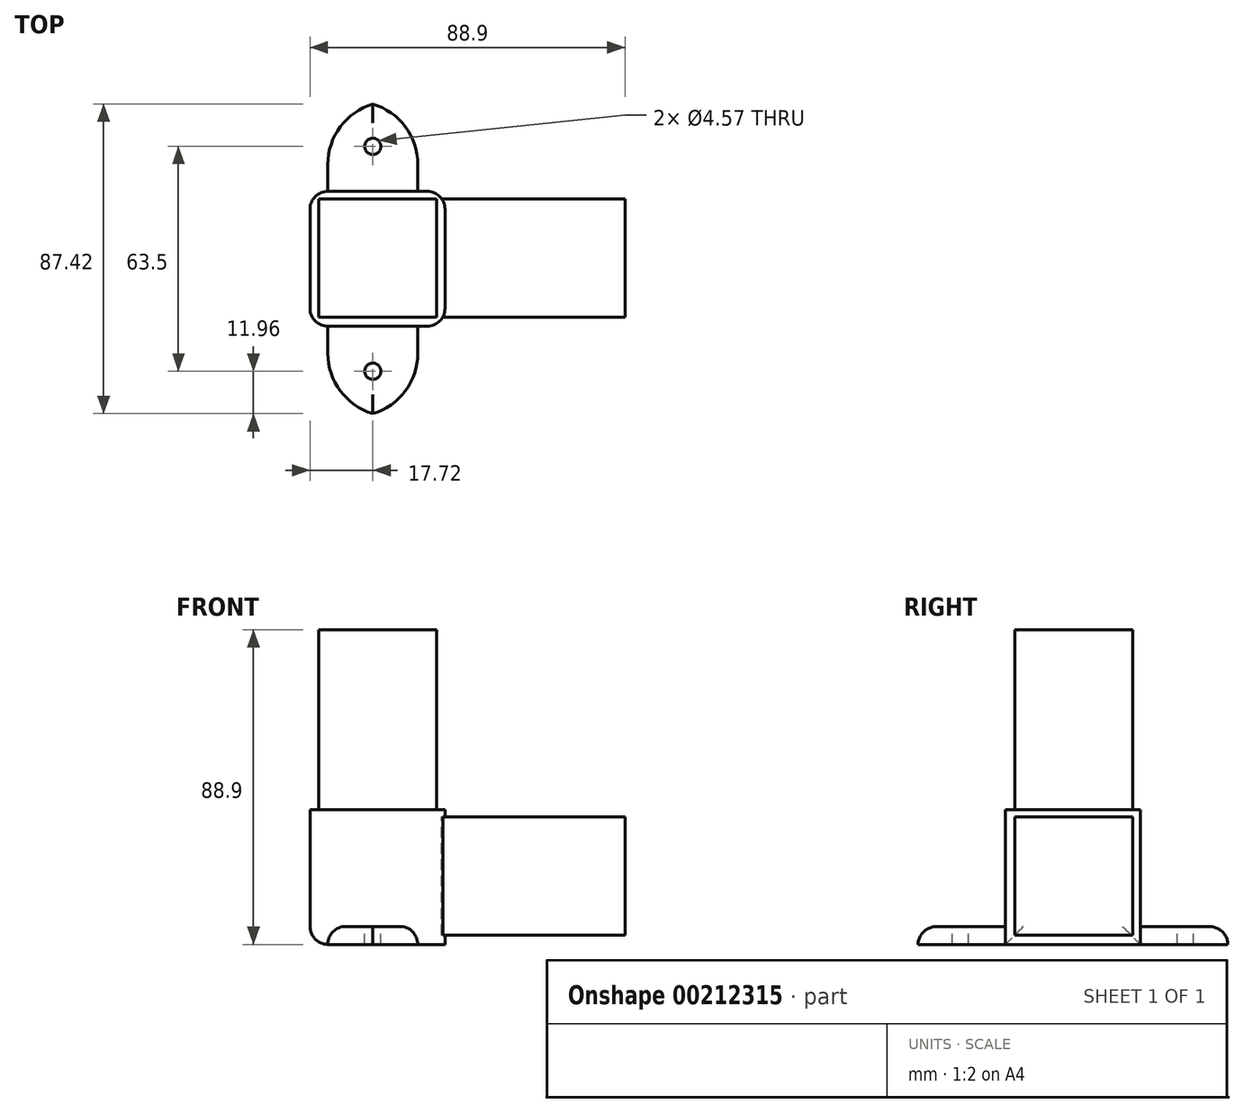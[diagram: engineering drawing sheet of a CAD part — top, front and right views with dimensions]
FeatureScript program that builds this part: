
annotation { "Feature Type Name" : "Feature", "Feature Type Description" : "" }
export const myFeature = defineFeature(function(context is Context, id is Id, definition is map)
    precondition{}
    {
        {
            var Q0;
            Q0=qCreatedBy(makeId("Front.planeOp"),FACE);
            var sketch = newSketch(context, id + "F0", { "sketchPlane" : qUnion([Q0])});
            skLineSegment(sketch, "E0.bottom", {"start": v(0.35, 8.9) * mm, "end": v(38.45, 8.9) * mm});
            skLineSegment(sketch, "E0.top", {"start": v(0.35, -29.2) * mm, "end": v(38.45, -29.2) * mm});
            skLineSegment(sketch, "E0.left", {"start": v(0.35, 8.9) * mm, "end": v(0.35, -29.2) * mm});
            skLineSegment(sketch, "E0.right", {"start": v(38.45, 8.9) * mm, "end": v(38.45, -29.2) * mm});
            skSolve(sketch);
        }
        {
            var Q0;
            Q0=makeQuery(id+"F0.imprint","IMPRINT",FACE,{"disambiguationData":[TD([[makeQuery(id+"F0.imprint","IMPRINT",EDGE,{"derivedFrom":sQuery(id+"F0.wireOp",EDGE,"E0.bottom")}),-1.0]])]});
            extrude(context, id + "F1", {"entities" : qUnion([Q0]), "depth" : 38.1 * mm});
        }
        {
            var Q0;
            Q0=makeQuery(id+"F1.opExtrude","SWEPT_FACE",FACE,{"disambiguationData":[OSD([sQuery(id+"F0.wireOp",EDGE,"E0.right")])]});
            var sketch = newSketch(context, id + "F2", { "sketchPlane" : qUnion([Q0])});
            skLineSegment(sketch, "E1.bottom", {"start": v(-35.49, 6.76) * mm, "end": v(-2.15, 6.76) * mm});
            skLineSegment(sketch, "E1.top", {"start": v(-35.49, -26.58) * mm, "end": v(-2.15, -26.58) * mm});
            skLineSegment(sketch, "E1.left", {"start": v(-35.49, 6.76) * mm, "end": v(-35.49, -26.58) * mm});
            skLineSegment(sketch, "E1.right", {"start": v(-2.15, 6.76) * mm, "end": v(-2.15, -26.58) * mm});
            skSolve(sketch);
        }
        {
            var Q0;
            Q0 = qSketchRegion(id + "F2", true);
            extrude(context, id + "F3", {"entities" : qUnion([Q0]), "operationType" : NewBodyOperationType.ADD, "depth" : 50.8 * mm});
        }
        {
            var Q0;
            Q0=makeQuery(id+"F1.opExtrude","SWEPT_FACE",FACE,{"disambiguationData":[OSD([sQuery(id+"F0.wireOp",EDGE,"E0.bottom")])]});
            var sketch = newSketch(context, id + "F4", { "sketchPlane" : qUnion([Q0])});
            skLineSegment(sketch, "E2.bottom", {"start": v(2.78, -35.49) * mm, "end": v(36.12, -35.49) * mm});
            skLineSegment(sketch, "E2.top", {"start": v(2.78, -2.15) * mm, "end": v(36.12, -2.15) * mm});
            skLineSegment(sketch, "E2.left", {"start": v(2.78, -35.49) * mm, "end": v(2.78, -2.15) * mm});
            skLineSegment(sketch, "E2.right", {"start": v(36.12, -35.49) * mm, "end": v(36.12, -2.15) * mm});
            skSolve(sketch);
        }
        {
            var Q0;
            Q0=makeQuery(id+"F4.imprint","IMPRINT",FACE,{"disambiguationData":[TD([[makeQuery(id+"F4.imprint","IMPRINT",EDGE,{"derivedFrom":sQuery(id+"F4.wireOp",EDGE,"E2.bottom")}),1.0]])]});
            var Q1;
            Q1=sQuery(id+"F4.wireOp",EDGE,"E2.top");
            var Q2;
            Q2=sQuery(id+"F4.wireOp",EDGE,"E2.left");
            var Q3;
            Q3=sQuery(id+"F4.wireOp",EDGE,"E2.right");
            extrude(context, id + "F5", {"entities" : qUnion([Q0]), "surfaceEntities" : qUnion([Q1, Q2, Q3]), "depth" : 50.8 * mm});
        }
        {
            var Q0;
            Q0=makeQuery(id+"F1.opExtrude","SWEPT_FACE",FACE,{"disambiguationData":[OSD([sQuery(id+"F0.wireOp",EDGE,"E0.top")])]});
            var sketch = newSketch(context, id + "F6", { "sketchPlane" : qUnion([Q0])});
            skLineSegment(sketch, "E3.bottom", {"start": v(5.37, 38.1) * mm, "end": v(30.77, 38.1) * mm});
            skLineSegment(sketch, "E3.top", {"start": v(5.37, 63.5) * mm, "end": v(30.77, 63.5) * mm});
            skLineSegment(sketch, "E3.left", {"start": v(5.37, 38.1) * mm, "end": v(5.37, 63.5) * mm});
            skLineSegment(sketch, "E3.right", {"start": v(30.77, 38.1) * mm, "end": v(30.77, 63.5) * mm});
            skLineSegment(sketch, "E4.bottom", {"start": v(5.37, 0) * mm, "end": v(30.77, 0) * mm});
            skLineSegment(sketch, "E4.top", {"start": v(5.37, -25.4) * mm, "end": v(30.77, -25.4) * mm});
            skLineSegment(sketch, "E4.left", {"start": v(5.37, 0) * mm, "end": v(5.37, -25.4) * mm});
            skLineSegment(sketch, "E4.right", {"start": v(30.77, 0) * mm, "end": v(30.77, -25.4) * mm});
            skSolve(sketch);
        }
        {
            var Q0;
            Q0=makeQuery(id+"F6.imprint","IMPRINT",FACE,{"disambiguationData":[TD([[makeQuery(id+"F6.imprint","IMPRINT",EDGE,{"derivedFrom":sQuery(id+"F6.wireOp",EDGE,"E4.bottom")}),-1.0]])]});
            var Q1;
            Q1=makeQuery(id+"F6.imprint","IMPRINT",FACE,{"disambiguationData":[TD([[makeQuery(id+"F6.imprint","IMPRINT",EDGE,{"derivedFrom":sQuery(id+"F6.wireOp",EDGE,"E3.bottom")}),1.0]])]});
            extrude(context, id + "F7", {"entities" : qUnion([Q0, Q1]), "oppositeDirection" : true, "depth" : 5.08 * mm});
        }
        {
            var Q0;
            Q0=makeQuery(id+"F7.opExtrude","CAP_FACE",FACE,{"disambiguationData":[OSD([sQuery(id+"F6.wireOp",EDGE,"E3.bottom"),sQuery(id+"F6.wireOp",EDGE,"E3.top"),sQuery(id+"F6.wireOp",EDGE,"E3.left"),sQuery(id+"F6.wireOp",EDGE,"E3.right")])],"isStart":false});
            var sketch = newSketch(context, id + "F8", { "sketchPlane" : qUnion([Q0])});
            skCircle(sketch, "E5", {"center": v(18.07, -50.8) * mm, "radius": 2.29 * mm});
            skCircle(sketch, "E6", {"center": v(18.07, 12.7) * mm, "radius": 2.29 * mm});
            skSolve(sketch);
        }
        {
            var Q0;
            Q0 = qSketchRegion(id + "F8", true);
            extrude(context, id + "F9", {"entities" : qUnion([Q0]), "operationType" : NewBodyOperationType.REMOVE, "oppositeDirection" : true, "depth" : 83.82 * mm});
        }
        {
            var Q0;
            Q0=makeQuery(id+"F7.opExtrude","SWEPT_EDGE",EDGE,{"disambiguationData":[OSD([sQuery(id+"F6.wireOp",EDGE,"E4.top"),sQuery(id+"F6.wireOp",EDGE,"E4.left")])]});
            var Q1;
            Q1=makeQuery(id+"F7.opExtrude","SWEPT_EDGE",EDGE,{"disambiguationData":[OSD([sQuery(id+"F6.wireOp",EDGE,"E4.top"),sQuery(id+"F6.wireOp",EDGE,"E4.right")])]});
            var Q2;
            Q2=makeQuery(id+"F7.opExtrude","SWEPT_EDGE",EDGE,{"disambiguationData":[OSD([sQuery(id+"F6.wireOp",EDGE,"E3.top"),sQuery(id+"F6.wireOp",EDGE,"E3.left")])]});
            var Q3;
            Q3=makeQuery(id+"F7.opExtrude","SWEPT_EDGE",EDGE,{"disambiguationData":[OSD([sQuery(id+"F6.wireOp",EDGE,"E3.top"),sQuery(id+"F6.wireOp",EDGE,"E3.right")])]});
            fillet(context, id + "F10", {"entities" : qUnion([Q0, Q1, Q2, Q3]), "radius" : 17.78 * mm, "tangentPropagation" : true, "allowEdgeOverflow" : false});
        }
        {
            var Q0;
            Q0=makeQuery(id+"F1.opExtrude","CAP_EDGE",EDGE,{"disambiguationData":[OSD([sQuery(id+"F0.wireOp",EDGE,"E0.left")])],"isStart":true});
            var Q1;
            Q1=makeQuery(id+"F1.opExtrude","CAP_EDGE",EDGE,{"disambiguationData":[OSD([sQuery(id+"F0.wireOp",EDGE,"E0.right")])],"isStart":true});
            var Q2;
            Q2=makeQuery(id+"F1.opExtrude","CAP_EDGE",EDGE,{"disambiguationData":[OSD([sQuery(id+"F0.wireOp",EDGE,"E0.left")])],"isStart":false});
            var Q3;
            Q3=makeQuery(id+"F1.opExtrude","SWEPT_EDGE",EDGE,{"disambiguationData":[OSD([sQuery(id+"F0.wireOp",EDGE,"E0.top"),sQuery(id+"F0.wireOp",EDGE,"E0.left")])]});
            var Q4;
            Q4=makeQuery(id+"F1.opExtrude","CAP_EDGE",EDGE,{"disambiguationData":[OSD([sQuery(id+"F0.wireOp",EDGE,"E0.right")])],"isStart":false});
            var Q5;
            Q5=makeQuery(id+"F7.opExtrude","CAP_EDGE",EDGE,{"disambiguationData":[OSD([sQuery(id+"F6.wireOp",EDGE,"E4.right")])],"isStart":false});
            var Q6;
            Q6=makeQuery(id+"F7.opExtrude","CAP_EDGE",EDGE,{"disambiguationData":[OSD([sQuery(id+"F6.wireOp",EDGE,"E4.left")])],"isStart":false});
            var Q7;
            Q7=makeQuery(id+"F7.opExtrude","CAP_EDGE",EDGE,{"disambiguationData":[OSD([sQuery(id+"F6.wireOp",EDGE,"E3.right")])],"isStart":false});
            var Q8;
            Q8=makeQuery(id+"F7.opExtrude","CAP_EDGE",EDGE,{"disambiguationData":[OSD([sQuery(id+"F6.wireOp",EDGE,"E3.left")])],"isStart":false});
            fillet(context, id + "F11", {"entities" : qUnion([Q0, Q1, Q2, Q3, Q4, Q5, Q6, Q7, Q8]), "radius" : 5.08 * mm, "tangentPropagation" : true, "allowEdgeOverflow" : false});
        }
    });
